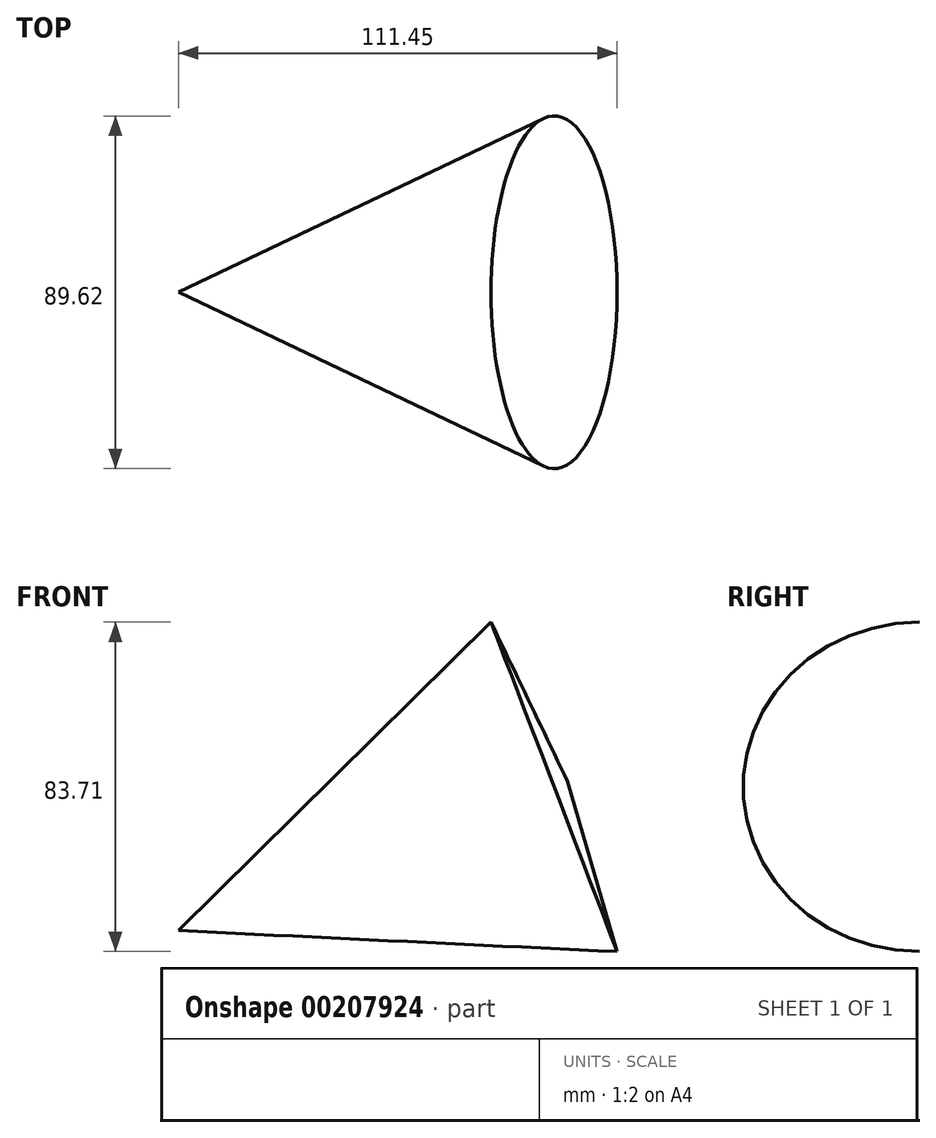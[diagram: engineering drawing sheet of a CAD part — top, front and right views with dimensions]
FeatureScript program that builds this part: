
annotation { "Feature Type Name" : "Feature", "Feature Type Description" : "" }
export const myFeature = defineFeature(function(context is Context, id is Id, definition is map)
    precondition{}
    {
        {
            var Q0;
            Q0=qCreatedBy(makeId("Front.planeOp"),FACE);
            var sketch = newSketch(context, id + "F0", { "sketchPlane" : qUnion([Q0])});
            skLineSegment(sketch, "E0", {"start": v(-66.28, -55.08) * mm, "end": v(32.62, -17.25) * mm});
            skLineSegment(sketch, "E1", {"start": v(32.62, -17.25) * mm, "end": v(45.17, -60.43) * mm});
            skLineSegment(sketch, "E2", {"start": v(45.17, -60.43) * mm, "end": v(-66.28, -55.08) * mm});
            skSolve(sketch);
        }
        {
            var Q0;
            Q0=makeQuery(id+"F0.imprint","IMPRINT",FACE,{"disambiguationData":[TD([[makeQuery(id+"F0.imprint","IMPRINT",EDGE,{"derivedFrom":sQuery(id+"F0.wireOp",EDGE,"E0")}),-1.0]])]});
            var Q1;
            Q1=sQuery(id+"F0.wireOp",EDGE,"E0");
            revolve(context, id + "F1", {"entities" : qUnion([Q0]), "axis" : qUnion([Q1]), "revolveType" : RevolveType.FULL});
        }
    });
